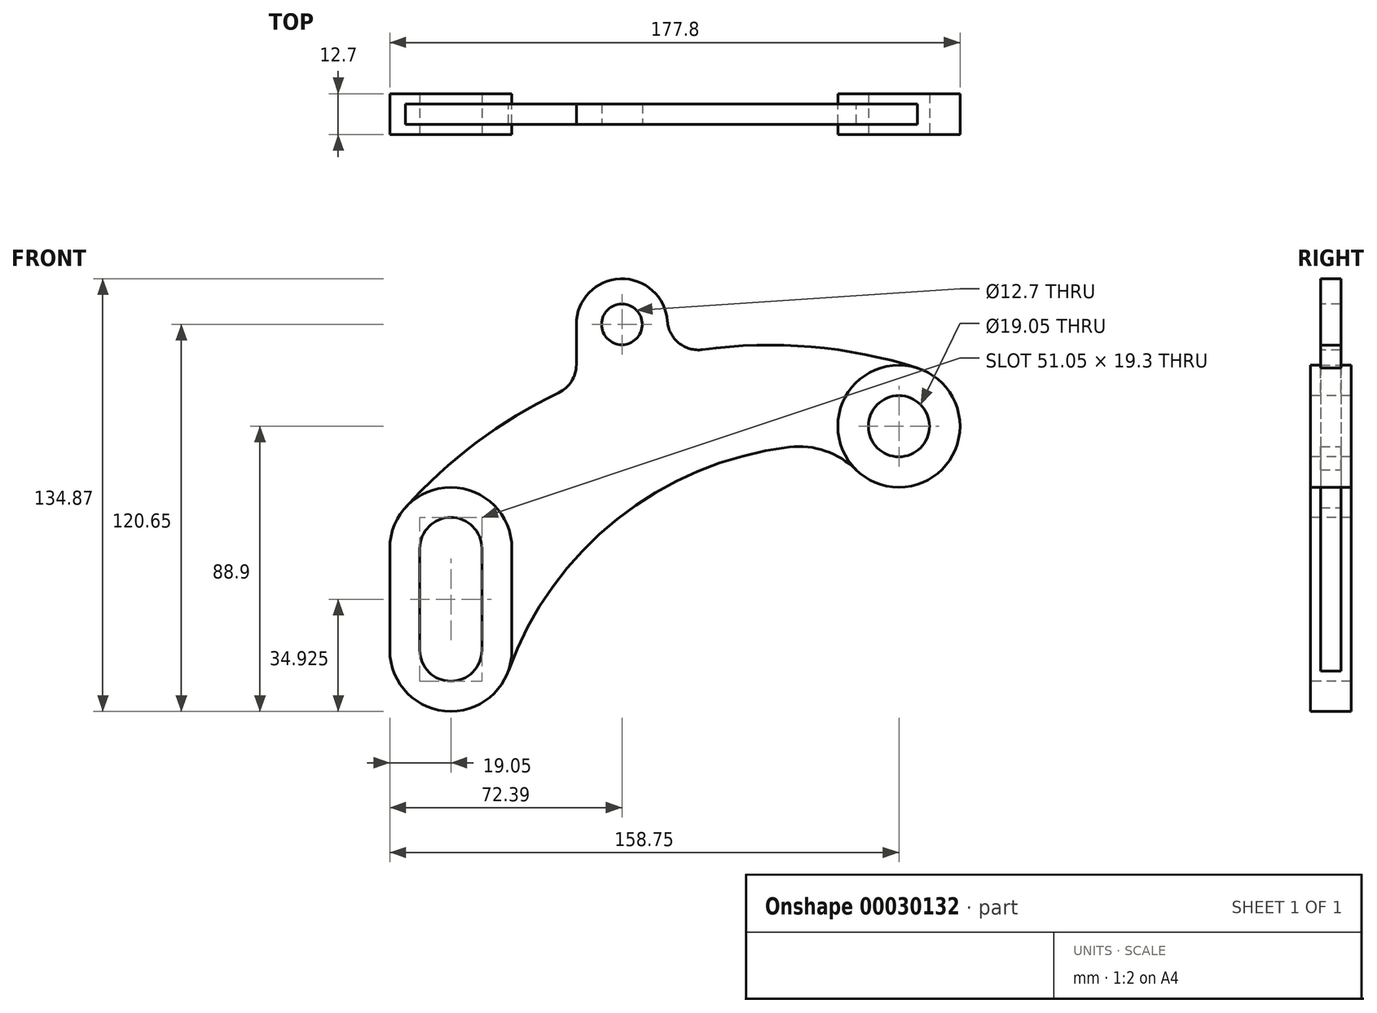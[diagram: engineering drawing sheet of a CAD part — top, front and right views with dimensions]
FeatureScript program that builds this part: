
annotation { "Feature Type Name" : "Feature", "Feature Type Description" : "" }
export const myFeature = defineFeature(function(context is Context, id is Id, definition is map)
    precondition{}
    {
        {
            var Q0;
            Q0=qCreatedBy(makeId("Front.planeOp"),FACE);
            var sketch = newSketch(context, id + "F0", { "sketchPlane" : qUnion([Q0])});
            skArc(sketch, "E0", {"start": v(19.05, 0) * mm, "mid": v(0, 19.05) * mm, "end": v(-19.05, 0) * mm});
            skLineSegment(sketch, "E1", {"start": v(-19.05, 0) * mm, "end": v(-19.05, -31.75) * mm});
            skArc(sketch, "E2", {"start": v(-19.05, -31.75) * mm, "mid": v(0, -50.8) * mm, "end": v(19.05, -31.75) * mm});
            skLineSegment(sketch, "E3", {"start": v(19.05, 0) * mm, "end": v(19.05, -31.75) * mm});
            skCircle(sketch, "E4", {"center": v(139.7, 38.1) * mm, "radius": 19.05 * mm});
            skArc(sketch, "E5", {"start": v(145.47, 56.26) * mm, "mid": v(59.22, 58.04) * mm, "end": v(-14.19, 12.71) * mm});
            skArc(sketch, "E6", {"start": v(126.37, 24.5) * mm, "mid": v(116.77, 30.4) * mm, "end": v(105.56, 31.57) * mm});
            skArc(sketch, "E7", {"start": v(105.56, 31.57) * mm, "mid": v(51.85, 9.11) * mm, "end": v(17.92, -38.2) * mm});
            skCircle(sketch, "E8", {"center": v(53.34, 69.85) * mm, "radius": 14.22 * mm});
            skLineSegment(sketch, "E9", {"start": v(39.12, 69.85) * mm, "end": v(39.12, 51.02) * mm});
            skLineSegment(sketch, "E10", {"start": v(67.56, 69.85) * mm, "end": v(67.56, 60.07) * mm});
            skSolve(sketch);
        }
        {
            var Q0;
            {var subQ3=sQuery(id+"F0.wireOp",EDGE,"E1");Q0=makeQuery(id+"F0.imprint","IMPRINT",FACE,{"disambiguationData":[TD([[makeQuery(id+"F0.imprint","IMPRINT",EDGE,{"derivedFrom":subQ3}),1.0]])]});}
            var Q1;
            {var subQ0=sQuery(id+"F0.wireOp",EDGE,"E4");var subQ2=makeQuery(id+"F0.imprint","INTERSECT",VERTEX,{"derivedFrom":[subQ0,sQuery(id+"F0.wireOp",EDGE,"E5")]});Q1=makeQuery(id+"F0.imprint","IMPRINT",FACE,{"disambiguationData":[TD([[makeQuery(id+"F0.imprint","IMPRINT",EDGE,{"disambiguationData":[TD([[subQ2,-1.0]])],"derivedFrom":subQ0}),1.0]])]});}
            extrude(context, id + "F1", {"entities" : qUnion([Q0, Q1]), "endBound" : BoundingType.SYMMETRIC, "depth" : 12.7 * mm});
        }
        {
            var Q0;
            {var subQ4=sQuery(id+"F0.wireOp",EDGE,"E3");Q0=makeQuery(id+"F0.imprint","IMPRINT",FACE,{"disambiguationData":[TD([[makeQuery(id+"F0.imprint","IMPRINT",EDGE,{"derivedFrom":subQ4}),1.0]])]});}
            var Q1;
            {var subQ0=sQuery(id+"F0.wireOp",EDGE,"E9");Q1=makeQuery(id+"F0.imprint","IMPRINT",FACE,{"disambiguationData":[TD([[makeQuery(id+"F0.imprint","IMPRINT",EDGE,{"derivedFrom":subQ0}),1.0]])]});}
            var Q2;
            {var subQ0=sQuery(id+"F0.wireOp",EDGE,"E8");var subQ1=sQuery(id+"F0.wireOp",EDGE,"E5");var subQ2=makeQuery(id+"F0.imprint","INTERSECT",VERTEX,{"disambiguationData":[OD(0.0)],"derivedFrom":[subQ1,subQ0]});Q2=makeQuery(id+"F0.imprint","IMPRINT",FACE,{"disambiguationData":[TD([[makeQuery(id+"F0.imprint","IMPRINT",EDGE,{"disambiguationData":[TD([[subQ2,-1.0]])],"derivedFrom":subQ1}),-1.0]])]});}
            var Q3;
            {var subQ0=sQuery(id+"F0.wireOp",EDGE,"E8");var subQ1=sQuery(id+"F0.wireOp",EDGE,"E5");var subQ3=makeQuery(id+"F0.imprint","INTERSECT",VERTEX,{"disambiguationData":[OD(0.0)],"derivedFrom":[subQ1,subQ0]});Q3=makeQuery(id+"F0.imprint","IMPRINT",FACE,{"disambiguationData":[TD([[makeQuery(id+"F0.imprint","IMPRINT",EDGE,{"disambiguationData":[TD([[subQ3,-1.0]])],"derivedFrom":subQ1}),1.0]])]});}
            var Q4;
            {var subQ0=sQuery(id+"F0.wireOp",EDGE,"E10");Q4=makeQuery(id+"F0.imprint","IMPRINT",FACE,{"disambiguationData":[TD([[makeQuery(id+"F0.imprint","IMPRINT",EDGE,{"derivedFrom":subQ0}),-1.0]])]});}
            extrude(context, id + "F2", {"entities" : qUnion([Q0, Q1, Q2, Q3, Q4]), "endBound" : BoundingType.SYMMETRIC, "depth" : 6.35 * mm});
        }
        {
            var Q0;
            Q0=makeQuery(id+"F1.opExtrude","CAP_FACE",FACE,{"disambiguationData":[OSD([sQuery(id+"F0.wireOp",EDGE,"E4")])],"isStart":false});
            var sketch = newSketch(context, id + "F3", { "sketchPlane" : qUnion([Q0])});
            skPoint(sketch, "E11", {"position": v(139.7, 38.1) * mm});
            skSolve(sketch);
        }
        {
            var Q0;
            Q0=sQuery(id+"F3.wireOp",VERTEX,"E11");
            var Q1;
            Q1=makeQuery(id+"F1.opExtrude","SWEPT_BODY",BODY,{"disambiguationData":[OSD([sQuery(id+"F0.wireOp",EDGE,"E4")])]});
            hole(context, id + "F4", {"style" : HoleStyle.SIMPLE, "holeDiameter" : 19.05 * mm, "endStyle" : HoleEndStyle.THROUGH, "locations" : qUnion([Q0]), "scope" : qUnion([Q1])});
        }
        {
            var Q0;
            Q0=makeQuery(id+"F1.opExtrude","CAP_FACE",FACE,{"disambiguationData":[OSD([sQuery(id+"F0.wireOp",EDGE,"E0"),sQuery(id+"F0.wireOp",EDGE,"E1"),sQuery(id+"F0.wireOp",EDGE,"E2"),sQuery(id+"F0.wireOp",EDGE,"E3")])],"isStart":false});
            var sketch = newSketch(context, id + "F5", { "sketchPlane" : qUnion([Q0])});
            skArc(sketch, "E12", {"start": v(9.65, 0) * mm, "mid": v(0, 9.65) * mm, "end": v(-9.65, 0) * mm});
            skArc(sketch, "E13", {"start": v(-9.65, -31.75) * mm, "mid": v(0, -41.4) * mm, "end": v(9.65, -31.75) * mm});
            skLineSegment(sketch, "E14", {"start": v(-9.65, 0) * mm, "end": v(-9.65, -31.75) * mm});
            skLineSegment(sketch, "E15", {"start": v(9.65, 0) * mm, "end": v(9.65, -31.75) * mm});
            skSolve(sketch);
        }
        {
            var Q0;
            Q0=makeQuery(id+"F5.imprint","IMPRINT",FACE,{"disambiguationData":[TD([[makeQuery(id+"F5.imprint","IMPRINT",EDGE,{"derivedFrom":sQuery(id+"F5.wireOp",EDGE,"E12")}),1.0]])]});
            extrude(context, id + "F6", {"entities" : qUnion([Q0]), "operationType" : NewBodyOperationType.REMOVE, "endBound" : BoundingType.UP_TO_NEXT, "oppositeDirection" : true, "depth" : 25.4 * mm});
        }
        {
            var Q0;
            Q0=makeQuery(id+"F2.opExtrude","SWEPT_EDGE",EDGE,{"disambiguationData":[OSD([sQuery(id+"F0.wireOp",EDGE,"E5"),sQuery(id+"F0.wireOp",EDGE,"E10")])]});
            var Q1;
            Q1=makeQuery(id+"F2.opExtrude","SWEPT_EDGE",EDGE,{"disambiguationData":[OSD([sQuery(id+"F0.wireOp",EDGE,"E5"),sQuery(id+"F0.wireOp",EDGE,"E9")])]});
            fillet(context, id + "F7", {"entities" : qUnion([Q0, Q1]), "radius" : 9.65 * mm, "allowEdgeOverflow" : false});
        }
        {
            var Q0;
            Q0=makeQuery(id+"F2.opExtrude","CAP_FACE",FACE,{"disambiguationData":[OSD([sQuery(id+"F0.wireOp",EDGE,"E0"),sQuery(id+"F0.wireOp",EDGE,"E2"),sQuery(id+"F0.wireOp",EDGE,"E3"),sQuery(id+"F0.wireOp",EDGE,"E4"),sQuery(id+"F0.wireOp",EDGE,"E5"),sQuery(id+"F0.wireOp",EDGE,"E6"),sQuery(id+"F0.wireOp",EDGE,"E7"),sQuery(id+"F0.wireOp",EDGE,"E8"),sQuery(id+"F0.wireOp",EDGE,"E9"),sQuery(id+"F0.wireOp",EDGE,"E10")])],"isStart":false});
            var sketch = newSketch(context, id + "F8", { "sketchPlane" : qUnion([Q0])});
            skPoint(sketch, "E16", {"position": v(53.34, 69.85) * mm});
            skSolve(sketch);
        }
        {
            var Q0;
            Q0=sQuery(id+"F8.wireOp",VERTEX,"E16");
            var Q1;
            Q1=makeQuery(id+"F2.opExtrude","SWEPT_BODY",BODY,{"disambiguationData":[OSD([sQuery(id+"F0.wireOp",EDGE,"E0"),sQuery(id+"F0.wireOp",EDGE,"E2"),sQuery(id+"F0.wireOp",EDGE,"E3"),sQuery(id+"F0.wireOp",EDGE,"E4"),sQuery(id+"F0.wireOp",EDGE,"E5"),sQuery(id+"F0.wireOp",EDGE,"E6"),sQuery(id+"F0.wireOp",EDGE,"E7"),sQuery(id+"F0.wireOp",EDGE,"E8"),sQuery(id+"F0.wireOp",EDGE,"E9"),sQuery(id+"F0.wireOp",EDGE,"E10")])]});
            hole(context, id + "F9", {"style" : HoleStyle.SIMPLE, "holeDiameter" : 12.7 * mm, "endStyle" : HoleEndStyle.THROUGH, "locations" : qUnion([Q0]), "scope" : qUnion([Q1])});
        }
    });
